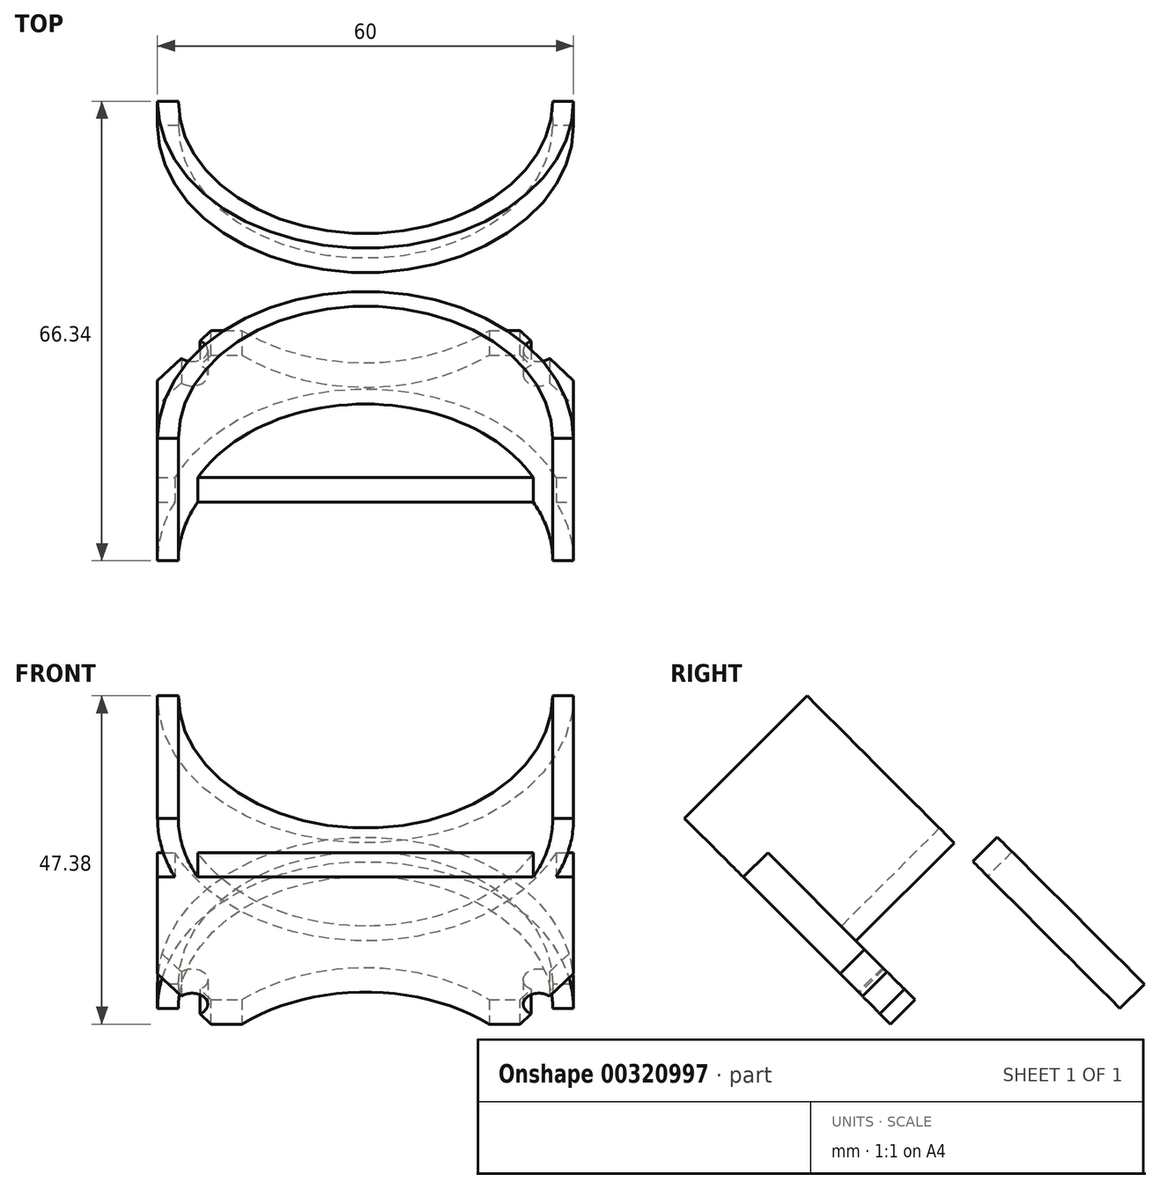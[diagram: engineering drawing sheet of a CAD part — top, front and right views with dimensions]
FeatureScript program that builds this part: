
annotation { "Feature Type Name" : "Feature", "Feature Type Description" : "" }
export const myFeature = defineFeature(function(context is Context, id is Id, definition is map)
    precondition{}
    {
        {
            var Q0;
            Q0=qCreatedBy(makeId("Top.planeOp"),FACE);
            var sketch = newSketch(context, id + "F0", { "sketchPlane" : qUnion([Q0])});
            skLineSegment(sketch, "E0.bottom", {"start": v(-30, 9.76) * mm, "end": v(-17.82, 9.76) * mm});
            skLineSegment(sketch, "E0.top", {"start": v(-30, -5.24) * mm, "end": v(30, -5.24) * mm});
            skLineSegment(sketch, "E0.left", {"start": v(-30, 9.76) * mm, "end": v(-30, -5.24) * mm});
            skLineSegment(sketch, "E0.right", {"start": v(30, 9.76) * mm, "end": v(30, -5.24) * mm});
            skCircle(sketch, "E1", {"center": v(-25, 5.7) * mm, "radius": 2.25 * mm});
            skCircle(sketch, "E2", {"center": v(25, 5.7) * mm, "radius": 2.25 * mm});
            skArc(sketch, "E3", {"start": v(-17.82, 9.76) * mm, "mid": v(0, 3.2) * mm, "end": v(17.82, 9.76) * mm});
            skLineSegment(sketch, "E4.trimOffspring", {"start": v(17.82, 9.76) * mm, "end": v(30, 9.76) * mm});
            skSolve(sketch);
        }
        {
            var Q0;
            Q0=qSketchRegion(id+"F0",true);
            extrude(context, id + "F1", {"entities" : qUnion([Q0]), "depth" : 5 * mm});
        }
        {
            var Q0;
            Q0=qCreatedBy(makeId("Top.planeOp"),FACE);
            var sketch = newSketch(context, id + "F2", { "sketchPlane" : qUnion([Q0])});
            skArc(sketch, "E5", {"start": v(27, -32.24) * mm, "mid": v(0, -5.24) * mm, "end": v(-27, -32.24) * mm});
            skArc(sketch, "E6.0", {"start": v(30, -32.24) * mm, "mid": v(0, -2.24) * mm, "end": v(-30, -32.24) * mm});
            skLineSegment(sketch, "E7", {"start": v(-27, -32.24) * mm, "end": v(-30, -32.24) * mm});
            skLineSegment(sketch, "E8", {"start": v(27, -32.24) * mm, "end": v(30, -32.24) * mm});
            skLineSegment(sketch, "E9.0.0", {"start": v(30, -5.24) * mm, "end": v(30, 9.76) * mm, "construction": true});
            skLineSegment(sketch, "E9.0.1", {"start": v(30, 9.76) * mm, "end": v(17.82, 9.76) * mm, "construction": true});
            skArc(sketch, "E9.0.2", {"start": v(17.82, 9.76) * mm, "mid": v(0, 3.2) * mm, "end": v(-17.82, 9.76) * mm, "construction": true});
            skLineSegment(sketch, "E9.0.3", {"start": v(-17.82, 9.76) * mm, "end": v(-30, 9.76) * mm, "construction": true});
            skLineSegment(sketch, "E9.0.4", {"start": v(-30, 9.76) * mm, "end": v(-30, -5.24) * mm, "construction": true});
            skLineSegment(sketch, "E9.0.5", {"start": v(-30, -5.24) * mm, "end": v(30, -5.24) * mm, "construction": true});
            skSolve(sketch);
        }
        {
            var Q0;
            Q0=qSketchRegion(id+"F2",true);
            extrude(context, id + "F3", {"entities" : qUnion([Q0]), "depth" : 25 * mm});
        }
        {
            var Q0;
            Q0=makeQuery(id+"F1.opExtrude","SWEPT_FACE",FACE,{"disambiguationData":[OSD([sQuery(id+"F0.wireOp",EDGE,"E0.top")])]});
            var sketch = newSketch(context, id + "F4", { "sketchPlane" : qUnion([Q0])});
            skLineSegment(sketch, "E10.0.0", {"start": v(-30, 0) * mm, "end": v(30, 0) * mm});
            skLineSegment(sketch, "E10.0.1", {"start": v(30, 0) * mm, "end": v(30, 5) * mm});
            skLineSegment(sketch, "E10.0.2", {"start": v(30, 5) * mm, "end": v(-30, 5) * mm});
            skLineSegment(sketch, "E10.0.3", {"start": v(-30, 5) * mm, "end": v(-30, 0) * mm});
            skSolve(sketch);
        }
        {
            var Q0;
            Q0=qSketchRegion(id+"F4",true);
            extrude(context, id + "F5", {"entities" : qUnion([Q0]), "operationType" : NewBodyOperationType.ADD, "depth" : 15 * mm});
        }
        {
            var Q0;
            Q0=makeQuery(id+"F5.boolean.opBoolean","MERGE",FACE,{"derivedFrom":[makeQuery(id+"F1.opExtrude","CAP_FACE",FACE,{"disambiguationData":[OSD([sQuery(id+"F0.wireOp",EDGE,"E0.bottom"),sQuery(id+"F0.wireOp",EDGE,"E0.top"),sQuery(id+"F0.wireOp",EDGE,"E0.left"),sQuery(id+"F0.wireOp",EDGE,"E0.right"),sQuery(id+"F0.wireOp",EDGE,"E1"),sQuery(id+"F0.wireOp",EDGE,"E2"),sQuery(id+"F0.wireOp",EDGE,"E3"),sQuery(id+"F0.wireOp",EDGE,"E4.trimOffspring")])],"isStart":true}),makeQuery(id+"F5.opExtrude","SWEPT_FACE",FACE,{"disambiguationData":[OSD([sQuery(id+"F4.wireOp",EDGE,"E10.0.0")])]})]});
            var sketch = newSketch(context, id + "F6", { "sketchPlane" : qUnion([Q0])});
            skArc(sketch, "E11.0", {"start": v(30, 32.24) * mm, "mid": v(0, 2.24) * mm, "end": v(-30, 32.24) * mm, "construction": true});
            skLineSegment(sketch, "E12", {"start": v(0, 2.24) * mm, "end": v(-49.4, 2.24) * mm});
            skSolve(sketch);
        }
        {
            var Q0;
            Q0=makeQuery(id+"F1.opExtrude","SWEPT_BODY",BODY,{"disambiguationData":[OSD([sQuery(id+"F0.wireOp",EDGE,"E0.bottom"),sQuery(id+"F0.wireOp",EDGE,"E0.top"),sQuery(id+"F0.wireOp",EDGE,"E0.left"),sQuery(id+"F0.wireOp",EDGE,"E0.right"),sQuery(id+"F0.wireOp",EDGE,"E1"),sQuery(id+"F0.wireOp",EDGE,"E2"),sQuery(id+"F0.wireOp",EDGE,"E3"),sQuery(id+"F0.wireOp",EDGE,"E4.trimOffspring")])]});
            var Q1;
            Q1=sQuery(id+"F6.wireOp",EDGE,"E12");
            transform(context, id + "F7", {"entities" : qUnion([Q0]), "transformType" : TransformType.ROTATION, "transformAxis" : qUnion([Q1]), "angle" : 45 * degree, "makeCopy" : false});
        }
        {
            var Q0;
            Q0=makeQuery(id+"F3.opExtrude","CAP_FACE",FACE,{"disambiguationData":[OSD([sQuery(id+"F2.wireOp",EDGE,"E5"),sQuery(id+"F2.wireOp",EDGE,"E6.0"),sQuery(id+"F2.wireOp",EDGE,"E7"),sQuery(id+"F2.wireOp",EDGE,"E8")])],"isStart":false});
            var sketch = newSketch(context, id + "F8", { "sketchPlane" : qUnion([Q0])});
            skArc(sketch, "E13.0", {"start": v(27, -32.24) * mm, "mid": v(0, -5.24) * mm, "end": v(-27, -32.24) * mm});
            skLineSegment(sketch, "E14", {"start": v(-27, -32.24) * mm, "end": v(27, -32.24) * mm});
            skSolve(sketch);
        }
        {
            var Q0;
            Q0=qSketchRegion(id+"F8",true);
            extrude(context, id + "F9", {"entities" : qUnion([Q0]), "operationType" : NewBodyOperationType.REMOVE, "oppositeDirection" : true, "depth" : 25 * mm});
        }
        {
            var Q0;
            Q0=makeQuery(id+"F3.opExtrude","CAP_FACE",FACE,{"disambiguationData":[OSD([sQuery(id+"F2.wireOp",EDGE,"E5"),sQuery(id+"F2.wireOp",EDGE,"E6.0"),sQuery(id+"F2.wireOp",EDGE,"E7"),sQuery(id+"F2.wireOp",EDGE,"E8")])],"isStart":false});
            var sketch = newSketch(context, id + "F10", { "sketchPlane" : qUnion([Q0])});
            skArc(sketch, "E15.0", {"start": v(-21.56, -11.38) * mm, "mid": v(-27.81, -20.99) * mm, "end": v(-30, -32.24) * mm});
            skLineSegment(sketch, "E16", {"start": v(-21.56, -11.38) * mm, "end": v(-30.12, 0) * mm});
            skLineSegment(sketch, "E17", {"start": v(-30.12, 0) * mm, "end": v(-30, -32.24) * mm});
            skLineSegment(sketch, "E18", {"start": v(0, -32.24) * mm, "end": v(0, -13.64) * mm, "construction": true});
            skPoint(sketch, "E19.orphan", {"position": v(30, -32.24) * mm});
            skLineSegment(sketch, "E20.MirrorCS", {"start": v(30.12, 0) * mm, "end": v(30, -32.24) * mm});
            skLineSegment(sketch, "E21.MirrorCS", {"start": v(21.56, -11.38) * mm, "end": v(30.12, 0) * mm});
            skArc(sketch, "E22.MirrorCS", {"start": v(21.56, -11.38) * mm, "mid": v(27.81, -20.99) * mm, "end": v(30, -32.24) * mm});
            skSolve(sketch);
        }
        {
            var Q0;
            Q0=qSketchRegion(id+"F10",true);
            extrude(context, id + "F11", {"entities" : qUnion([Q0]), "operationType" : NewBodyOperationType.REMOVE, "oppositeDirection" : true, "depth" : 29.2 * mm});
        }
        {
            var Q0;
            Q0=qCreatedBy(makeId("Right.planeOp"),FACE);
            var sketch = newSketch(context, id + "F12", { "sketchPlane" : qUnion([Q0])});
            skLineSegment(sketch, "E23.0", {"start": v(-11.38, 9.14) * mm, "end": v(-2.24, 0) * mm});
            skLineSegment(sketch, "E24.0", {"start": v(-32.24, 9.14) * mm, "end": v(-32.24, 0) * mm});
            skLineSegment(sketch, "E25", {"start": v(-11.38, 9.14) * mm, "end": v(-32.24, 9.14) * mm});
            skLineSegment(sketch, "E26", {"start": v(-32.24, 0) * mm, "end": v(-2.24, 0) * mm});
            skPoint(sketch, "E27.orphan", {"position": v(-0.16, -2.08) * mm});
            skPoint(sketch, "E28.orphan", {"position": v(-32.24, 25) * mm});
            skSolve(sketch);
        }
        {
            var Q0;
            Q0=qSketchRegion(id+"F12",true);
            extrude(context, id + "F13", {"entities" : qUnion([Q0]), "operationType" : NewBodyOperationType.REMOVE, "endBound" : BoundingType.SYMMETRIC, "oppositeDirection" : true, "depth" : 84.4 * mm});
        }
        {
            var Q0;
            Q0=makeQuery(id+"F3.opExtrude","CAP_FACE",FACE,{"disambiguationData":[OSD([sQuery(id+"F2.wireOp",EDGE,"E5"),sQuery(id+"F2.wireOp",EDGE,"E6.0"),sQuery(id+"F2.wireOp",EDGE,"E7"),sQuery(id+"F2.wireOp",EDGE,"E8")])],"isStart":false});
            var sketch = newSketch(context, id + "F14", { "sketchPlane" : qUnion([Q0])});
            skLineSegment(sketch, "E29.0.0", {"start": v(27, -32.24) * mm, "end": v(30, -32.24) * mm});
            skArc(sketch, "E29.0.1", {"start": v(30, -32.24) * mm, "mid": v(0, -2.24) * mm, "end": v(-30, -32.24) * mm});
            skLineSegment(sketch, "E29.0.2", {"start": v(-30, -32.24) * mm, "end": v(-27, -32.24) * mm});
            skArc(sketch, "E29.0.3", {"start": v(-27, -32.24) * mm, "mid": v(0, -5.24) * mm, "end": v(27, -32.24) * mm});
            skSolve(sketch);
        }
        {
            var Q0;
            Q0=qSketchRegion(id+"F14",true);
            extrude(context, id + "F15", {"entities" : qUnion([Q0]), "operationType" : NewBodyOperationType.ADD, "depth" : 5 * mm});
        }
    });
